# Revit family: Plumbing-Faucet-Sloan-Valve-EFX-275
name_source: partatom
category: Plumbing Fixtures
units: mm (PartAtom-declared; Revit-internal decimal feet)

## family parameters
Cut with Voids When Loaded = No
Host = Face
OmniClass Number = 23.45.55.14
OmniClass Title = Single Faucets
Part Type = Normal
Room Calculation Point = No
Round Connector Dimension = Use Diameter
Shared = No

## types (1)
- Plumbing-Faucet-Sloan-Valve-EFX-275
    Assembly Code = D2010
    CW Connection = Yes
    CWFU = 1.5
    Cold Water Connection Diameter = 0"
    Default Elevation = 0"
    Depth = 6 1/2"
    Description = Solar Power Supply, Back-Check Tee, Polished Chrome Finish, 1.5 gpm, Aerated (installed) or Laminar (in box) Spray, Infrared Sensor, BASYS® Solar-Powered Deck-Mounted Mid Body Faucet.
    Edition number = 1
    HW Connection = Yes
    HWFU = 1.5
    Height = 6 1/2"
    Hot Water Connection Diameter = 0"
    Keynote = 15410
    Manufacturer = Sloan Valve
    Model = Model not specified - Load type catalog!
    Part Number = 3324074
    Product Material = Sloan Valve - Finish - Polished Chrome
    Product data url = https://bimobject.com
    URL = www.sloanvalve.com
    Valve Pressure Drop = 0.00 psi
    Vent Connection = No
    WFU = 0
    Waste Connection = No
    Water Flow = 2 GPM
    z_Offset = 0"
    z_Trim Plate 4 = No
    z_Trim Plate 8 = No

## geometry (parser evidence)
native form markers: Sweep x8
no freeform markers — native parametric forms only
